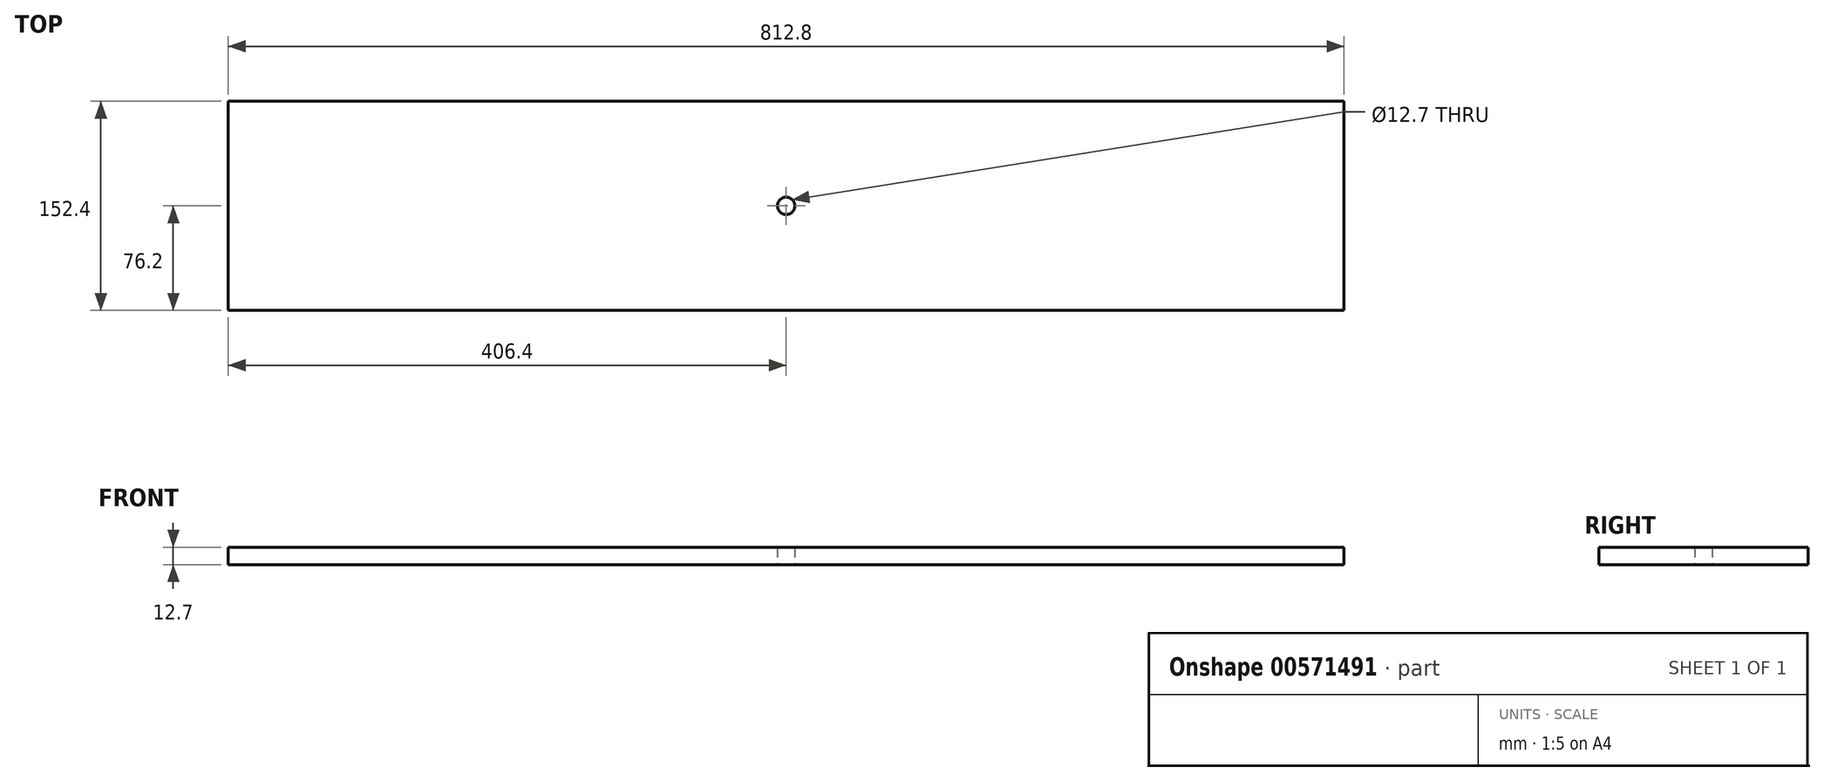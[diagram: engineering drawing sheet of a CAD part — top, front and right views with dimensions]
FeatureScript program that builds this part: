
annotation { "Feature Type Name" : "Feature", "Feature Type Description" : "" }
export const myFeature = defineFeature(function(context is Context, id is Id, definition is map)
    precondition{}
    {
        {
            var Q0;
            Q0=qCreatedBy(makeId("Top.planeOp"),FACE);
            var sketch = newSketch(context, id + "F0", { "sketchPlane" : qUnion([Q0])});
            skLineSegment(sketch, "E0.bottom", {"start": v(406.4, -76.2) * mm, "end": v(-406.4, -76.2) * mm});
            skLineSegment(sketch, "E0.top", {"start": v(406.4, 76.2) * mm, "end": v(-406.4, 76.2) * mm});
            skLineSegment(sketch, "E0.left", {"start": v(406.4, -76.2) * mm, "end": v(406.4, 76.2) * mm});
            skLineSegment(sketch, "E0.right", {"start": v(-406.4, -76.2) * mm, "end": v(-406.4, 76.2) * mm});
            skPoint(sketch, "E0.middle", {"position": v(0, 0) * mm});
            skCircle(sketch, "E1", {"center": v(0, 0) * mm, "radius": 6.35 * mm});
            skSolve(sketch);
        }
        {
            var Q0;
            Q0 = qSketchRegion(id + "F0", true);
            extrude(context, id + "F1", {"entities" : qUnion([Q0]), "depth" : 12.7 * mm, "offsetDistance" : 25.4 * mm});
        }
    });
